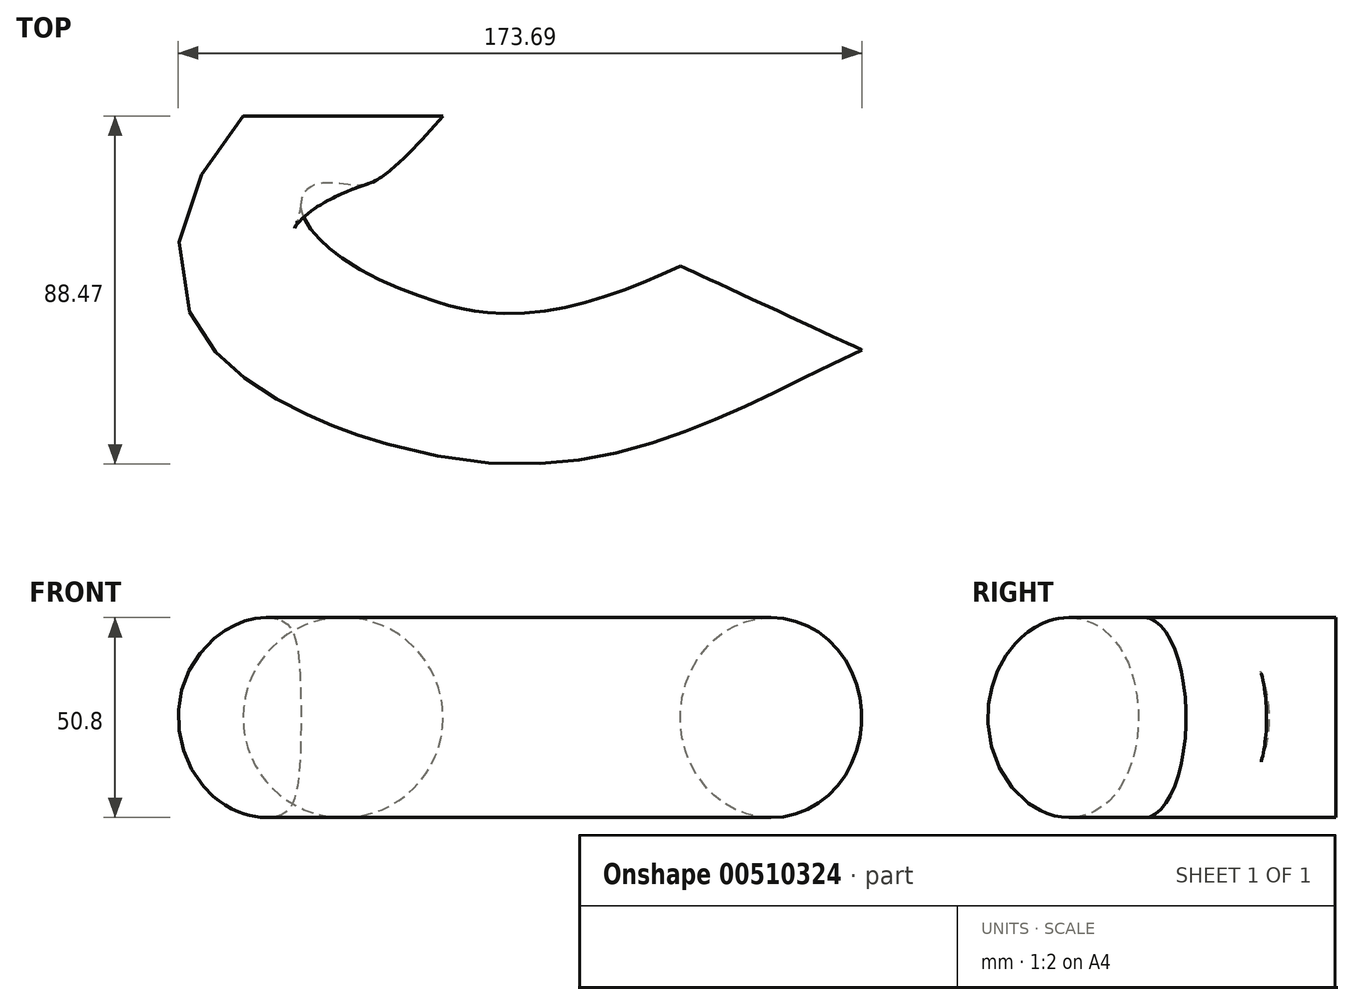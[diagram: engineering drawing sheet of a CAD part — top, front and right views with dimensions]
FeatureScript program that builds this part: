
annotation { "Feature Type Name" : "Feature", "Feature Type Description" : "" }
export const myFeature = defineFeature(function(context is Context, id is Id, definition is map)
    precondition{}
    {
        {
            var Q0;
            Q0=qCreatedBy(makeId("Front.planeOp"),FACE);
            var sketch = newSketch(context, id + "F0", { "sketchPlane" : qUnion([Q0])});
            skCircle(sketch, "E0", {"center": v(0, 0) * mm, "radius": 25.4 * mm});
            skSolve(sketch);
        }
        {
            var Q0;
            Q0=qCreatedBy(makeId("Top.planeOp"),FACE);
            var sketch = newSketch(context, id + "F1", { "sketchPlane" : qUnion([Q0])});
            skFitSpline(sketch, "E1", {"points": [v(0, 0) * mm, v(-18.67, -38.86) * mm, v(38.23, -67.63) * mm, v(108.73, -48.76) * mm], "startDerivative": vector(-119.8, -141.79) * mm, "endDerivative": vector(180.32, 84.08) * mm});
            skSolve(sketch);
        }
        {
            var Q0;
            Q0=makeQuery(id+"F0.imprint","IMPRINT",FACE,{"disambiguationData":[TD([[makeQuery(id+"F0.imprint","IMPRINT",EDGE,{"derivedFrom":sQuery(id+"F0.wireOp",EDGE,"E0")}),1.0]])]});
            var Q1;
            Q1=sQuery(id+"F1.wireOp",EDGE,"E1");
            sweep(context, id + "F2", {"profiles" : qUnion([Q0]), "path" : qUnion([Q1])});
        }
    });
